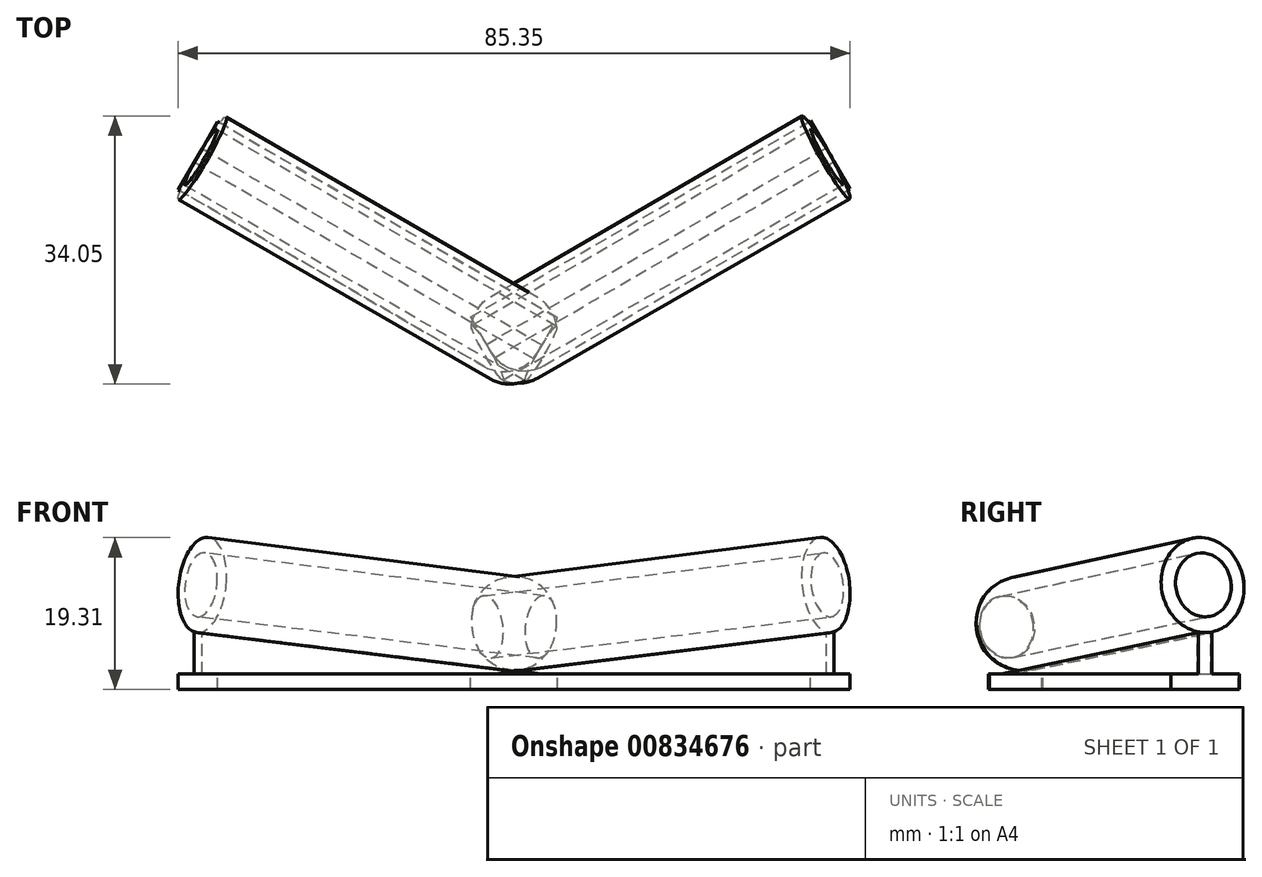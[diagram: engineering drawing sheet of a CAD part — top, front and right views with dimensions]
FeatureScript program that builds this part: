
annotation { "Feature Type Name" : "Feature", "Feature Type Description" : "" }
export const myFeature = defineFeature(function(context is Context, id is Id, definition is map)
    precondition{}
    {
        {
            var Q0;
            Q0=qCreatedBy(makeId("Front.planeOp"),FACE);
            var sketch = newSketch(context, id + "F0", { "sketchPlane" : qUnion([Q0])});
            skLineSegment(sketch, "E0", {"start": v(0, 16.98) * mm, "end": v(0, -4.1) * mm});
            skSolve(sketch);
        }
        {
            var Q0;
            Q0=qCreatedBy(makeId("Right.planeOp"),FACE);
            var Q1;
            Q1=sQuery(id+"F0.wireOp",EDGE,"E0");
            cPlane(context, id + "F1", {"entities" : qUnion([Q0, Q1]), "cplaneType" : CPlaneType.LINE_ANGLE, "offset" : 25 * mm, "angle" : 60 * degree, "width" : 150 * mm, "height" : 150 * mm});
        }
        {
            var Q0;
            Q0=qCreatedBy(id+"F1.planeOp",FACE);
            var sketch = newSketch(context, id + "F2", { "sketchPlane" : qUnion([Q0])});
            skLineSegment(sketch, "E1", {"start": v(3.39, 2) * mm, "end": v(3.39, 4) * mm});
            skLineSegment(sketch, "E2", {"start": v(3.39, 4) * mm, "end": v(3.39, 8) * mm});
            skLineSegment(sketch, "E3", {"start": v(3.39, 0) * mm, "end": v(3.39, 2) * mm});
            skLineSegment(sketch, "E4", {"start": v(0.39, 0) * mm, "end": v(50.25, 0) * mm});
            skLineSegment(sketch, "E5.MirrorCS", {"start": v(3.39, 8) * mm, "end": v(-46.38, 13.33) * mm});
            skLineSegment(sketch, "E6.MirrorCS", {"start": v(-46.48, 10.24) * mm, "end": v(-46.48, 14.24) * mm});
            skLineSegment(sketch, "E7.MirrorCS", {"start": v(3.39, 2) * mm, "end": v(-46.48, 7.24) * mm});
            skLineSegment(sketch, "E8.MirrorCS", {"start": v(3.39, 4) * mm, "end": v(-46.48, 9.24) * mm});
            skLineSegment(sketch, "E9.MirrorCS", {"start": v(-46.48, 3) * mm, "end": v(-46.48, 8.24) * mm});
            skLineSegment(sketch, "E10.MirrorCS", {"start": v(3.39, 0) * mm, "end": v(-46.48, 0) * mm});
            skLineSegment(sketch, "E11.MirrorCS", {"start": v(3.39, 2) * mm, "end": v(-46.48, 2) * mm});
            skLineSegment(sketch, "E12.MirrorCS", {"start": v(-46.48, 0) * mm, "end": v(-46.48, 3) * mm});
            skLineSegment(sketch, "E13.MirrorCS", {"start": v(-46.48, 8.24) * mm, "end": v(-46.48, 10.24) * mm});
            skSolve(sketch);
        }
        {
            var Q0;
            Q0=makeQuery(id+"F2.imprint","IMPRINT",FACE,{"disambiguationData":[TD([[makeQuery(id+"F2.imprint","IMPRINT",EDGE,{"derivedFrom":sQuery(id+"F2.wireOp",EDGE,"E7.MirrorCS")}),1.0]])]});
            extrude(context, id + "F3", {"entities" : qUnion([Q0]), "endBound" : BoundingType.SYMMETRIC, "depth" : 2 * mm, "offsetDistance" : 25 * mm});
        }
        {
            var Q0;
            {var subQ0=sQuery(id+"F2.wireOp",EDGE,"E3");Q0=makeQuery(id+"F2.imprint","IMPRINT",FACE,{"disambiguationData":[TD([[makeQuery(id+"F2.imprint","IMPRINT",EDGE,{"derivedFrom":subQ0}),1.0]])]});}
            extrude(context, id + "F4", {"entities" : qUnion([Q0]), "operationType" : NewBodyOperationType.ADD, "endBound" : BoundingType.SYMMETRIC, "depth" : 10 * mm, "offsetDistance" : 25 * mm});
        }
        {
            var Q0;
            {var subQ0=sQuery(id+"F2.wireOp",EDGE,"E8.MirrorCS");Q0=makeQuery(id+"F2.imprint","IMPRINT",FACE,{"disambiguationData":[TD([[makeQuery(id+"F2.imprint","IMPRINT",EDGE,{"derivedFrom":subQ0}),1.0]])]});}
            var Q1;
            {var subQ0=sQuery(id+"F2.wireOp",EDGE,"E7.MirrorCS");Q1=makeQuery(id+"F2.imprint","IMPRINT",FACE,{"disambiguationData":[TD([[makeQuery(id+"F2.imprint","IMPRINT",EDGE,{"derivedFrom":subQ0}),-1.0]])]});}
            var Q2;
            Q2=sQuery(id+"F2.wireOp",EDGE,"E5.MirrorCS");
            revolve(context, id + "F5", {"operationType" : NewBodyOperationType.ADD, "surfaceOperationType" : NewSurfaceOperationType.NEW, "entities" : qUnion([Q0, Q1]), "axis" : qUnion([Q2]), "revolveType" : RevolveType.FULL});
        }
        {
            var Q0;
            Q0=qCreatedBy(makeId("Right.planeOp"),FACE);
            var Q1;
            Q1=sQuery(id+"F0.wireOp",EDGE,"E0");
            cPlane(context, id + "F6", {"entities" : qUnion([Q0, Q1]), "cplaneType" : CPlaneType.LINE_ANGLE, "offset" : 25 * mm, "angle" : 60 * degree, "oppositeDirection" : true, "width" : 150 * mm, "height" : 150 * mm});
        }
        {
            var Q0;
            Q0=qCreatedBy(id+"F6.planeOp",FACE);
            var sketch = newSketch(context, id + "F7", { "sketchPlane" : qUnion([Q0])});
            skLineSegment(sketch, "E14", {"start": v(3.6, 2) * mm, "end": v(3.6, 4) * mm});
            skLineSegment(sketch, "E15", {"start": v(3.6, 4) * mm, "end": v(3.6, 8) * mm});
            skLineSegment(sketch, "E16", {"start": v(3.6, 0) * mm, "end": v(3.6, 2) * mm});
            skLineSegment(sketch, "E17", {"start": v(-0.2, 0) * mm, "end": v(49.67, 0) * mm});
            skLineSegment(sketch, "E18.MirrorCS", {"start": v(3.6, 8) * mm, "end": v(-46.16, 13.33) * mm});
            skLineSegment(sketch, "E19.MirrorCS", {"start": v(-46.25, 10.24) * mm, "end": v(-46.25, 14.24) * mm});
            skLineSegment(sketch, "E20.MirrorCS", {"start": v(3.6, 2) * mm, "end": v(-46.25, 7.24) * mm});
            skLineSegment(sketch, "E21.MirrorCS", {"start": v(3.6, 4) * mm, "end": v(-46.25, 9.24) * mm});
            skLineSegment(sketch, "E22.MirrorCS", {"start": v(-46.25, 3) * mm, "end": v(-46.25, 8.24) * mm});
            skLineSegment(sketch, "E23.MirrorCS", {"start": v(3.6, 0) * mm, "end": v(-46.25, 0) * mm});
            skLineSegment(sketch, "E24.MirrorCS", {"start": v(3.6, 2) * mm, "end": v(-46.25, 2) * mm});
            skLineSegment(sketch, "E25.MirrorCS", {"start": v(-46.25, 0) * mm, "end": v(-46.25, 2) * mm});
            skLineSegment(sketch, "E26.MirrorCS", {"start": v(-46.25, 8.24) * mm, "end": v(-46.25, 10.24) * mm});
            skLineSegment(sketch, "E27", {"start": v(-46.25, 2) * mm, "end": v(-46.25, 3) * mm});
            skSolve(sketch);
        }
        {
            var Q0;
            Q0=makeQuery(id+"F7.imprint","IMPRINT",FACE,{"disambiguationData":[TD([[makeQuery(id+"F7.imprint","IMPRINT",EDGE,{"derivedFrom":sQuery(id+"F7.wireOp",EDGE,"E20.MirrorCS")}),1.0]])]});
            extrude(context, id + "F8", {"entities" : qUnion([Q0]), "endBound" : BoundingType.SYMMETRIC, "depth" : 2 * mm, "offsetDistance" : 25 * mm});
        }
        {
            var Q0;
            {var subQ0=sQuery(id+"F7.wireOp",EDGE,"E16");Q0=makeQuery(id+"F7.imprint","IMPRINT",FACE,{"disambiguationData":[TD([[makeQuery(id+"F7.imprint","IMPRINT",EDGE,{"derivedFrom":subQ0}),1.0]])]});}
            extrude(context, id + "F9", {"entities" : qUnion([Q0]), "endBound" : BoundingType.SYMMETRIC, "depth" : 10 * mm, "offsetDistance" : 25 * mm});
        }
        {
            var Q0;
            Q0=makeQuery(id+"F7.imprint","IMPRINT",FACE,{"disambiguationData":[TD([[makeQuery(id+"F7.imprint","IMPRINT",EDGE,{"derivedFrom":sQuery(id+"F7.wireOp",EDGE,"E14")}),1.0]])]});
            var Q1;
            Q1=sQuery(id+"F7.wireOp",EDGE,"E18.MirrorCS");
            revolve(context, id + "F10", {"surfaceOperationType" : NewSurfaceOperationType.NEW, "entities" : qUnion([Q0]), "axis" : qUnion([Q1]), "revolveType" : RevolveType.FULL});
        }
        {
            var Q0;
            Q0=makeQuery(id+"F5.opRevolve","SWEPT_EDGE",EDGE,{"disambiguationData":[OSD([sQuery(id+"F2.wireOp",EDGE,"E1"),sQuery(id+"F2.wireOp",EDGE,"E3"),sQuery(id+"F2.wireOp",EDGE,"E7.MirrorCS"),sQuery(id+"F2.wireOp",EDGE,"E11.MirrorCS")])]});
            var Q1;
            Q1=makeQuery(id+"F10.opRevolve","SWEPT_EDGE",EDGE,{"disambiguationData":[OSD([sQuery(id+"F7.wireOp",EDGE,"E14"),sQuery(id+"F7.wireOp",EDGE,"E16"),sQuery(id+"F7.wireOp",EDGE,"E20.MirrorCS"),sQuery(id+"F7.wireOp",EDGE,"E24.MirrorCS")])]});
            var Q2;
            Q2=makeQuery(id+"F9.opExtrude","CAP_EDGE",EDGE,{"disambiguationData":[OSD([sQuery(id+"F7.wireOp",EDGE,"E16")])],"isStart":false});
            var Q3;
            Q3=makeQuery(id+"F4.opExtrude","CAP_EDGE",EDGE,{"disambiguationData":[OSD([sQuery(id+"F2.wireOp",EDGE,"E3")])],"isStart":true});
            fillet(context, id + "F11", {"entities" : qUnion([Q0, Q1, Q2, Q3]), "radius" : 5 * mm, "tangentPropagation" : true, "allowEdgeOverflow" : false});
        }
    });
